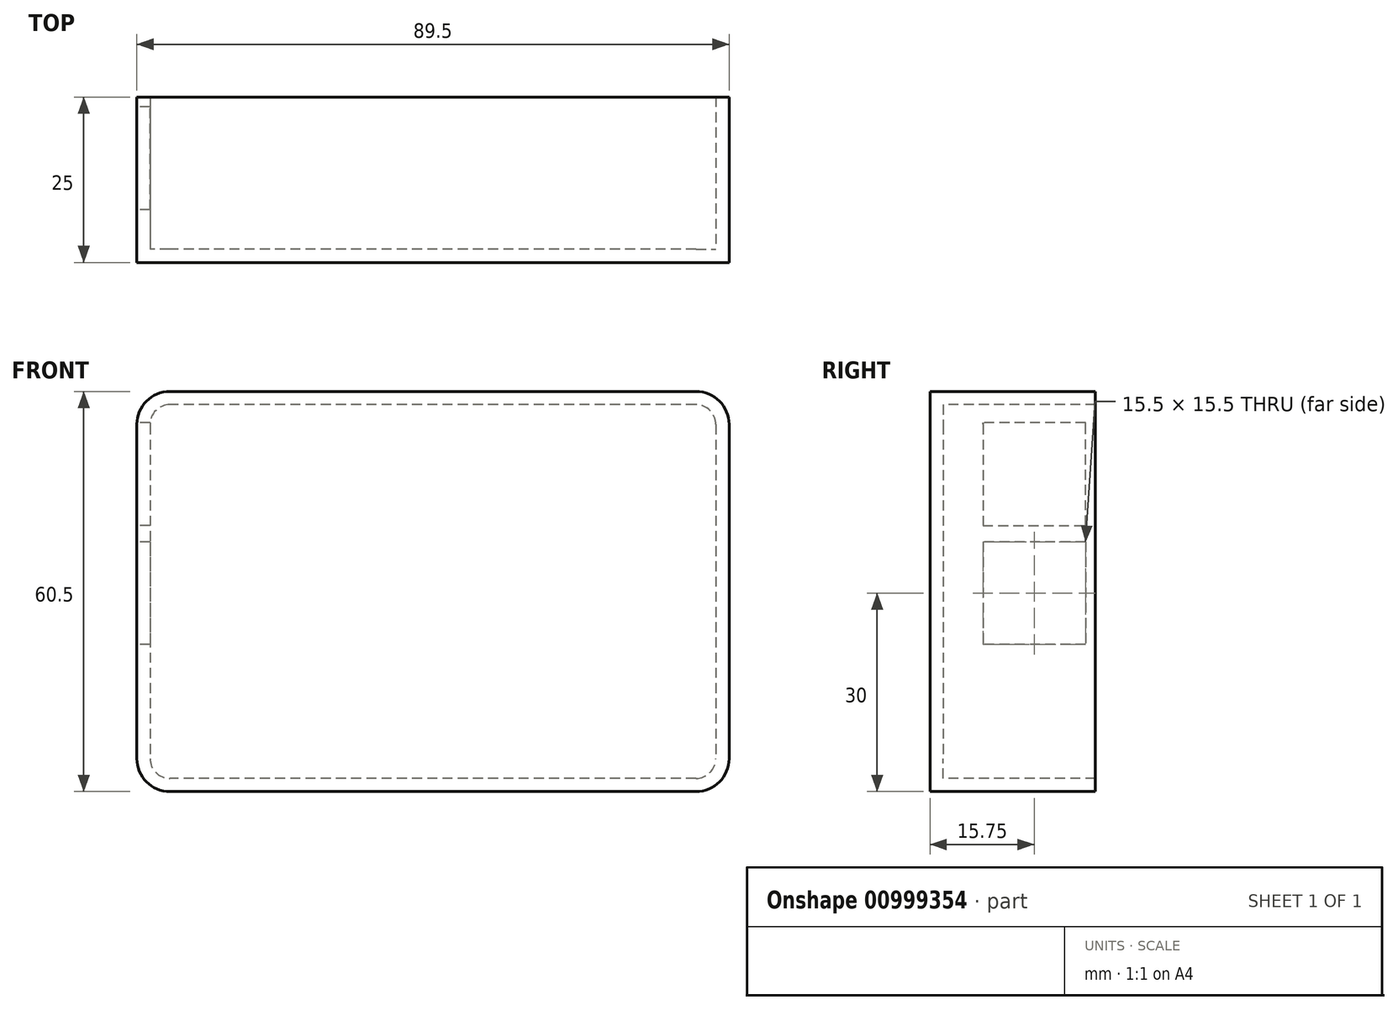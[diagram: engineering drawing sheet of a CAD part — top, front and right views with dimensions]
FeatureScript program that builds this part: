
annotation { "Feature Type Name" : "Feature", "Feature Type Description" : "" }
export const myFeature = defineFeature(function(context is Context, id is Id, definition is map)
    precondition{}
    {
        {
            var Q0;
            Q0=qCreatedBy(makeId("Front.planeOp"),FACE);
            var sketch = newSketch(context, id + "F0", { "sketchPlane" : qUnion([Q0])});
            skLineSegment(sketch, "E0.bottom", {"start": v(39.75, 28.25) * mm, "end": v(-39.75, 28.25) * mm});
            skLineSegment(sketch, "E0.top", {"start": v(39.75, -28.25) * mm, "end": v(-39.75, -28.25) * mm});
            skLineSegment(sketch, "E0.left", {"start": v(42.75, 25.25) * mm, "end": v(42.75, -25.25) * mm});
            skLineSegment(sketch, "E0.right", {"start": v(-42.75, 25.25) * mm, "end": v(-42.75, -25.25) * mm});
            skPoint(sketch, "E0.middle", {"position": v(0, 0) * mm});
            skPoint(sketch, "E1.visualSharp", {"position": v(42.75, 28.25) * mm});
            skArc(sketch, "E1.filletArc", {"start": v(42.75, 25.25) * mm, "mid": v(41.87, 27.37) * mm, "end": v(39.75, 28.25) * mm});
            skPoint(sketch, "E2.visualSharp", {"position": v(42.75, -28.25) * mm});
            skArc(sketch, "E2.filletArc", {"start": v(39.75, -28.25) * mm, "mid": v(41.87, -27.37) * mm, "end": v(42.75, -25.25) * mm});
            skPoint(sketch, "E3.visualSharp", {"position": v(-42.75, -28.25) * mm});
            skArc(sketch, "E3.filletArc", {"start": v(-42.75, -25.25) * mm, "mid": v(-41.87, -27.37) * mm, "end": v(-39.75, -28.25) * mm});
            skPoint(sketch, "E4.visualSharp", {"position": v(-42.75, 28.25) * mm});
            skArc(sketch, "E4.filletArc", {"start": v(-39.75, 28.25) * mm, "mid": v(-41.87, 27.37) * mm, "end": v(-42.75, 25.25) * mm});
            skArc(sketch, "E5.0", {"start": v(44.75, 25.25) * mm, "mid": v(43.29, 28.79) * mm, "end": v(39.75, 30.25) * mm});
            skLineSegment(sketch, "E5.1", {"start": v(44.75, 25.25) * mm, "end": v(44.75, -25.25) * mm});
            skLineSegment(sketch, "E5.2", {"start": v(39.75, 30.25) * mm, "end": v(-39.75, 30.25) * mm});
            skArc(sketch, "E5.3", {"start": v(39.75, -30.25) * mm, "mid": v(43.29, -28.79) * mm, "end": v(44.75, -25.25) * mm});
            skArc(sketch, "E5.4", {"start": v(-39.75, 30.25) * mm, "mid": v(-43.29, 28.79) * mm, "end": v(-44.75, 25.25) * mm});
            skLineSegment(sketch, "E5.5", {"start": v(-44.75, 25.25) * mm, "end": v(-44.75, -25.25) * mm});
            skArc(sketch, "E5.6", {"start": v(-44.75, -25.25) * mm, "mid": v(-43.29, -28.79) * mm, "end": v(-39.75, -30.25) * mm});
            skLineSegment(sketch, "E5.7", {"start": v(39.75, -30.25) * mm, "end": v(-39.75, -30.25) * mm});
            skSolve(sketch);
        }
        {
            var Q0;
            Q0=makeQuery(id+"F0.imprint","IMPRINT",FACE,{"disambiguationData":[TD([[makeQuery(id+"F0.imprint","IMPRINT",EDGE,{"derivedFrom":sQuery(id+"F0.wireOp",EDGE,"E0.bottom")}),-1.0]])]});
            var Q1;
            Q1=makeQuery(id+"F0.imprint","IMPRINT",FACE,{"disambiguationData":[TD([[makeQuery(id+"F0.imprint","IMPRINT",EDGE,{"derivedFrom":sQuery(id+"F0.wireOp",EDGE,"E0.bottom")}),1.0]])]});
            var Q2;
            Q2=sQuery(id+"F0.wireOp",EDGE,"E5.5");
            var Q3;
            Q3=sQuery(id+"F0.wireOp",EDGE,"E5.4");
            var Q4;
            Q4=sQuery(id+"F0.wireOp",EDGE,"E5.2");
            var Q5;
            Q5=sQuery(id+"F0.wireOp",EDGE,"E5.0");
            var Q6;
            Q6=sQuery(id+"F0.wireOp",EDGE,"E5.1");
            var Q7;
            Q7=sQuery(id+"F0.wireOp",EDGE,"E5.3");
            var Q8;
            Q8=sQuery(id+"F0.wireOp",EDGE,"E5.7");
            var Q9;
            Q9=sQuery(id+"F0.wireOp",EDGE,"E5.6");
            extrude(context, id + "F1", {"entities" : qUnion([Q0, Q1]), "surfaceEntities" : qUnion([Q2, Q3, Q4, Q5, Q6, Q7, Q8, Q9]), "depth" : 2 * mm, "offsetDistance" : 25 * mm});
        }
        {
            var Q0;
            Q0=makeQuery(id+"F0.imprint","IMPRINT",FACE,{"disambiguationData":[TD([[makeQuery(id+"F0.imprint","IMPRINT",EDGE,{"derivedFrom":sQuery(id+"F0.wireOp",EDGE,"E0.bottom")}),-1.0]])]});
            extrude(context, id + "F2", {"entities" : qUnion([Q0]), "operationType" : NewBodyOperationType.ADD, "oppositeDirection" : true, "depth" : 23 * mm, "offsetDistance" : 25 * mm});
        }
        {
            var Q0;
            {var subQ0=sQuery(id+"F0.wireOp",EDGE,"E5.5");Q0=makeQuery(id+"F2.boolean.opBoolean","MERGE",FACE,{"derivedFrom":[makeQuery(id+"F1.opExtrude","SWEPT_FACE",FACE,{"disambiguationData":[OSD([subQ0])]}),makeQuery(id+"F2.opExtrude","SWEPT_FACE",FACE,{"disambiguationData":[OSD([subQ0])]})]});}
            var sketch = newSketch(context, id + "F3", { "sketchPlane" : qUnion([Q0])});
            skPoint(sketch, "E6.0", {"position": v(0, 28.25) * mm});
            skLineSegment(sketch, "E7", {"start": v(0, 28.25) * mm, "end": v(0, 25.5) * mm, "construction": true});
            skLineSegment(sketch, "E8", {"start": v(0, 25.5) * mm, "end": v(-6, 25.5) * mm, "construction": true});
            skLineSegment(sketch, "E9.bottom", {"start": v(-6, 25.5) * mm, "end": v(-21.5, 25.5) * mm});
            skLineSegment(sketch, "E9.top", {"start": v(-6, 10) * mm, "end": v(-21.5, 10) * mm});
            skLineSegment(sketch, "E9.left", {"start": v(-6, 25.5) * mm, "end": v(-6, 10) * mm});
            skLineSegment(sketch, "E9.right", {"start": v(-21.5, 25.5) * mm, "end": v(-21.5, 10) * mm});
            skLineSegment(sketch, "E10.bottom", {"start": v(-21.5, 7.5) * mm, "end": v(-6, 7.5) * mm});
            skLineSegment(sketch, "E10.top", {"start": v(-21.5, -8) * mm, "end": v(-6, -8) * mm});
            skLineSegment(sketch, "E10.left", {"start": v(-21.5, 7.5) * mm, "end": v(-21.5, -8) * mm});
            skLineSegment(sketch, "E10.right", {"start": v(-6, 7.5) * mm, "end": v(-6, -8) * mm});
            skSolve(sketch);
        }
        {
            var Q0;
            Q0 = qSketchRegion(id + "F3", true);
            extrude(context, id + "F4", {"entities" : qUnion([Q0]), "operationType" : NewBodyOperationType.REMOVE, "oppositeDirection" : true, "depth" : 25 * mm, "offsetDistance" : 25 * mm});
        }
    });
